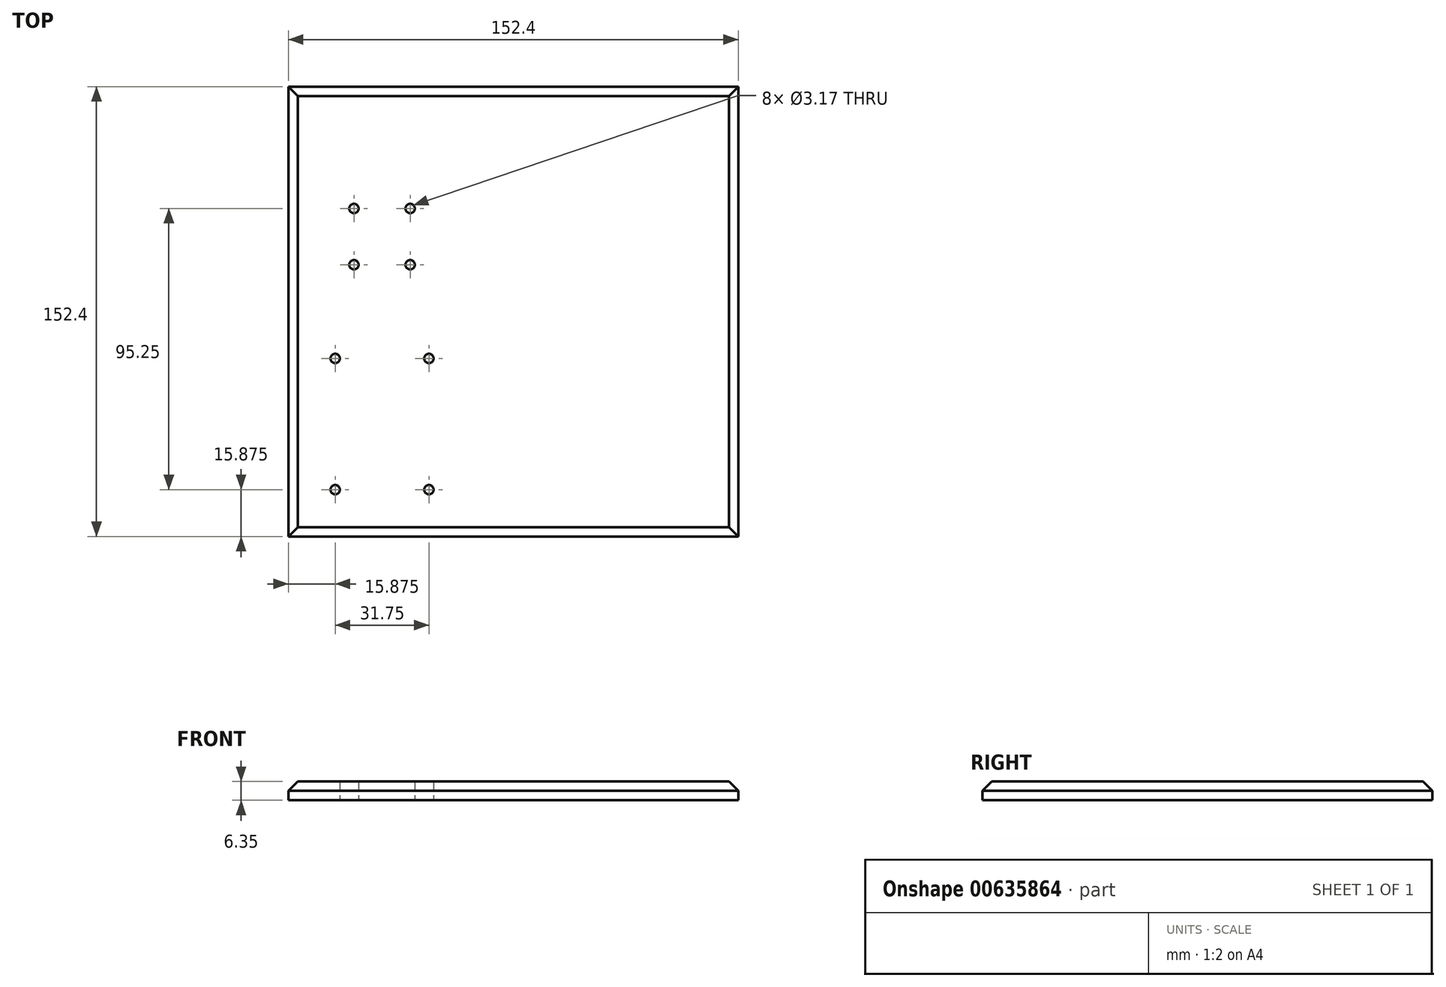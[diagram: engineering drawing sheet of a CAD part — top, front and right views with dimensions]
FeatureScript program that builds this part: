
annotation { "Feature Type Name" : "Feature", "Feature Type Description" : "" }
export const myFeature = defineFeature(function(context is Context, id is Id, definition is map)
    precondition{}
    {
        {
            var Q0;
            Q0=qCreatedBy(makeId("Top.planeOp"),FACE);
            var sketch = newSketch(context, id + "F0", { "sketchPlane" : qUnion([Q0])});
            skLineSegment(sketch, "E0.bottom", {"start": v(0, 0) * mm, "end": v(152.4, 0) * mm});
            skLineSegment(sketch, "E0.top", {"start": v(0, 152.4) * mm, "end": v(152.4, 152.4) * mm});
            skLineSegment(sketch, "E0.left", {"start": v(0, 0) * mm, "end": v(0, 152.4) * mm});
            skLineSegment(sketch, "E0.right", {"start": v(152.4, 0) * mm, "end": v(152.4, 152.4) * mm});
            skLineSegment(sketch, "E1", {"start": v(0, 12.7) * mm, "end": v(12.7, 12.7) * mm, "construction": true});
            skLineSegment(sketch, "E2", {"start": v(12.7, 12.7) * mm, "end": v(12.7, 0) * mm, "construction": true});
            skLineSegment(sketch, "E3.bottom", {"start": v(12.7, 12.7) * mm, "end": v(50.8, 12.7) * mm, "construction": true});
            skLineSegment(sketch, "E3.top", {"start": v(12.7, 63.5) * mm, "end": v(50.8, 63.5) * mm, "construction": true});
            skLineSegment(sketch, "E3.left", {"start": v(12.7, 12.7) * mm, "end": v(12.7, 63.5) * mm, "construction": true});
            skLineSegment(sketch, "E3.right", {"start": v(50.8, 12.7) * mm, "end": v(50.8, 63.5) * mm, "construction": true});
            skLineSegment(sketch, "E4", {"start": v(12.7, 60.33) * mm, "end": v(15.87, 60.33) * mm, "construction": true});
            skLineSegment(sketch, "E5", {"start": v(15.88, 60.33) * mm, "end": v(15.88, 63.5) * mm, "construction": true});
            skLineSegment(sketch, "E6", {"start": v(12.7, 15.88) * mm, "end": v(15.87, 15.88) * mm, "construction": true});
            skLineSegment(sketch, "E7", {"start": v(15.88, 15.88) * mm, "end": v(15.88, 12.7) * mm, "construction": true});
            skLineSegment(sketch, "E8", {"start": v(47.63, 12.7) * mm, "end": v(47.63, 15.88) * mm, "construction": true});
            skLineSegment(sketch, "E9", {"start": v(47.62, 15.88) * mm, "end": v(50.8, 15.88) * mm, "construction": true});
            skLineSegment(sketch, "E10", {"start": v(47.63, 63.5) * mm, "end": v(47.63, 60.33) * mm, "construction": true});
            skLineSegment(sketch, "E11", {"start": v(47.62, 60.33) * mm, "end": v(50.8, 60.33) * mm, "construction": true});
            skCircle(sketch, "E12", {"center": v(15.87, 60.33) * mm, "radius": 1.59 * mm});
            skCircle(sketch, "E13", {"center": v(15.87, 15.88) * mm, "radius": 1.59 * mm});
            skCircle(sketch, "E14", {"center": v(47.62, 15.88) * mm, "radius": 1.59 * mm});
            skCircle(sketch, "E15", {"center": v(47.62, 60.33) * mm, "radius": 1.59 * mm});
            skLineSegment(sketch, "E16.bottom", {"start": v(19.05, 88.9) * mm, "end": v(44.45, 88.9) * mm, "construction": true});
            skLineSegment(sketch, "E16.top", {"start": v(19.05, 114.3) * mm, "end": v(44.45, 114.3) * mm, "construction": true});
            skLineSegment(sketch, "E16.left", {"start": v(19.05, 88.9) * mm, "end": v(19.05, 114.3) * mm, "construction": true});
            skLineSegment(sketch, "E16.right", {"start": v(44.45, 88.9) * mm, "end": v(44.45, 114.3) * mm, "construction": true});
            skLineSegment(sketch, "E17", {"start": v(19.05, 101.6) * mm, "end": v(44.45, 101.6) * mm, "construction": true});
            skLineSegment(sketch, "E18", {"start": v(41.28, 88.9) * mm, "end": v(41.28, 92.08) * mm, "construction": true});
            skLineSegment(sketch, "E19", {"start": v(41.28, 92.08) * mm, "end": v(44.45, 92.08) * mm, "construction": true});
            skLineSegment(sketch, "E20", {"start": v(19.05, 92.08) * mm, "end": v(22.23, 92.08) * mm, "construction": true});
            skLineSegment(sketch, "E21", {"start": v(22.22, 92.08) * mm, "end": v(22.22, 88.9) * mm, "construction": true});
            skLineSegment(sketch, "E22", {"start": v(19.05, 111.13) * mm, "end": v(22.23, 111.13) * mm, "construction": true});
            skLineSegment(sketch, "E23", {"start": v(22.22, 111.13) * mm, "end": v(22.22, 114.3) * mm, "construction": true});
            skLineSegment(sketch, "E24", {"start": v(44.45, 111.13) * mm, "end": v(41.28, 111.13) * mm, "construction": true});
            skLineSegment(sketch, "E25", {"start": v(41.28, 111.13) * mm, "end": v(41.28, 114.3) * mm, "construction": true});
            skCircle(sketch, "E26", {"center": v(22.23, 111.13) * mm, "radius": 1.59 * mm});
            skCircle(sketch, "E27", {"center": v(41.28, 111.13) * mm, "radius": 1.59 * mm});
            skCircle(sketch, "E28", {"center": v(22.23, 92.08) * mm, "radius": 1.59 * mm});
            skCircle(sketch, "E29", {"center": v(41.28, 92.08) * mm, "radius": 1.59 * mm});
            skLineSegment(sketch, "E30", {"start": v(31.75, 88.9) * mm, "end": v(31.75, 63.5) * mm, "construction": true});
            skSolve(sketch);
        }
        {
            var Q0;
            Q0=makeQuery(id+"F0.imprint","IMPRINT",FACE,{"disambiguationData":[TD([[makeQuery(id+"F0.imprint","IMPRINT",EDGE,{"derivedFrom":sQuery(id+"F0.wireOp",EDGE,"E0.bottom")}),1.0]])]});
            extrude(context, id + "F1", {"entities" : qUnion([Q0]), "depth" : 6.35 * mm, "offsetDistance" : 25.4 * mm});
        }
        {
            var Q0;
            Q0=makeQuery(id+"F1.opExtrude","CAP_EDGE",EDGE,{"disambiguationData":[OSD([sQuery(id+"F0.wireOp",EDGE,"E0.left")])],"isStart":false});
            var Q1;
            Q1=makeQuery(id+"F1.opExtrude","CAP_EDGE",EDGE,{"disambiguationData":[OSD([sQuery(id+"F0.wireOp",EDGE,"E0.bottom")])],"isStart":false});
            var Q2;
            Q2=makeQuery(id+"F1.opExtrude","CAP_EDGE",EDGE,{"disambiguationData":[OSD([sQuery(id+"F0.wireOp",EDGE,"E0.right")])],"isStart":false});
            var Q3;
            Q3=makeQuery(id+"F1.opExtrude","CAP_EDGE",EDGE,{"disambiguationData":[OSD([sQuery(id+"F0.wireOp",EDGE,"E0.top")])],"isStart":false});
            chamfer(context, id + "F2", {"entities" : qUnion([Q0, Q1, Q2, Q3]), "width" : 3.17 * mm, "tangentPropagation" : true});
        }
    });
